# Revit family: Valve_Rough-Thermostatic-DXV-D35005511.191
name_source: partatom
category: Plumbing Fixtures
units: mm (PartAtom-declared; Revit-internal decimal feet)

## family parameters
Cut with Voids When Loaded = No
Host = Face
OmniClass Number = 23.45.05.14.17
OmniClass Title = Showers
Part Type = Normal
Room Calculation Point = No
Round Connector Dimension = Use Radius
Shared = Yes

## types (1)
- D35005511.191
    Assembly Code = D2010710
    Back to Finished Wall = 3"
    Back to Finished Wall Constraint = 3"
    CW Connection = Yes
    CWFU = 2
    Default Elevation = 0"
    Description = 2-HANDLE THERMOSTATIC ROUGH WITH VOLUME CONTROL
    Finish = Metal-DXV-Brass
    HW Connection = Yes
    HWFU = 3
    Height = 3 3/8"
    Hot/Cold Inlet to Wall = 3 11/16"
    Hot/Cold Inlet to Wall Constraint = 3 11/16"
    IAPMO Compliance = Meets or Exceeds ASME A112.18.1/CSA B125.1/ASSE 1016
    Installation Type = Wall Mounted
    Length = 1 3/4"
    Manufacturer = DXV
    Material = Metal-DXV-Brass
    Model = D35005511.191
    Price = Prices may vary. Please consult Manufacturer Representative for most up-to-date price list.
    Product Documentation Link = https://dxv01.blob.core.windows.net
    Product Page URL = https://www.dxv.com
    Tempered Water Connection Diameter = 1/2"
    Tempered Water Connection Radius = 1/4"
    Temperred Connection Width = 1 11/16"
    URL = https://www.dxv.com
    Vent Connection = No
    WFU = 4
    Waste Connection = No
    Width = 5 7/8"

## geometry (parser evidence)
native form markers: Sweep x3
no freeform markers — native parametric forms only
